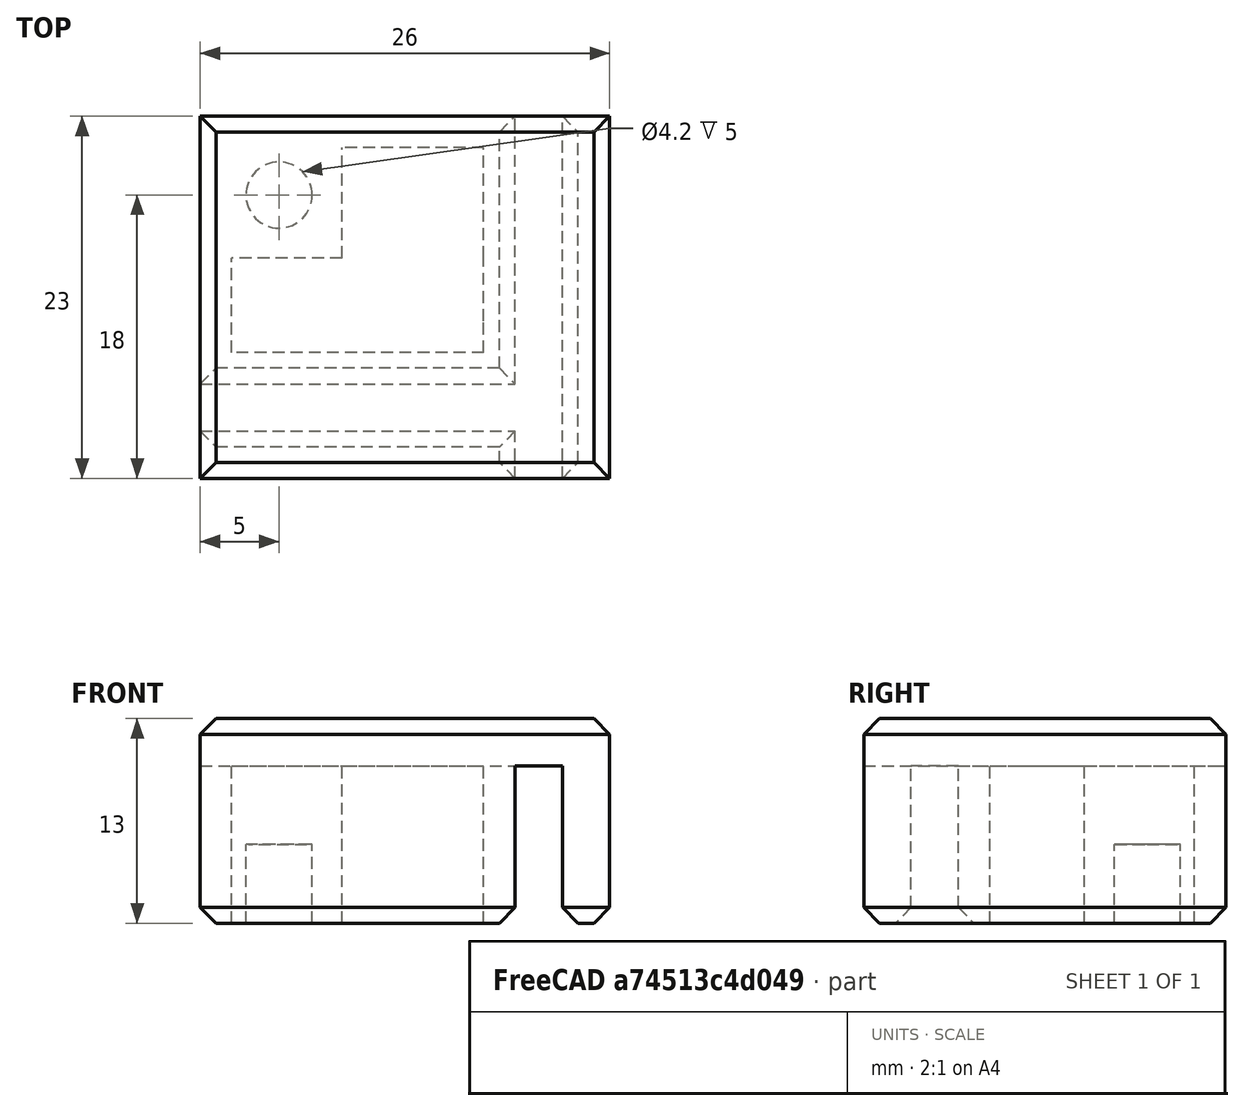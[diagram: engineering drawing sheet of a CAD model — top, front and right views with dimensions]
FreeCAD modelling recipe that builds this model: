
FCSTD DOCUMENT  (FreeCAD 0.16R6662 (Git))
Label: stangenhalter_eck
License: CreativeCommons Attribution-ShareAlike
LicenseURL: http://creativecommons.org/licenses/by-sa/4.0/
objects: Part::Cut×6, Part::Box×5, Part::Chamfer×3, Part::Cylinder×2
note: 16 computed .brp shape members not serialized (recipe doc carries the construction recipe); baked Part::Feature solids carry a one-line shape summary decoded from their .brp

FEATURE [Part::Box] Box  label="Cube"
  Height = 23
  Length = 26
  Placement = pos=(0,0,0) rot=(1,0,0;1.5708rad)
  Width = 13
FEATURE [Part::Cylinder] Cylinder
  Angle = 360
  Height = 10
  Placement = pos=(5,-5,-5) rot=(0,0,1;0rad)
  Radius = 2
FEATURE [Part::Box] Box001  label="Cube001"
  Height = 11
  Length = 3
  Placement = pos=(20,-24,-1) rot=(0,0,1;0rad)
  Width = 25
FEATURE [Part::Box] Box002  label="Cube002"
  Height = 11
  Length = 22
  Placement = pos=(-1,-20,-1) rot=(0,0,1;0rad)
  Width = 3
FEATURE [Part::Cut] Cut
  Base = -> Box
  Tool = -> Cylinder
FEATURE [Part::Cut] Cut001
  Base = -> Cut
  Tool = -> Box001
FEATURE [Part::Cut] Cut002
  Base = -> Cut001
  Tool = -> Box002
FEATURE [Part::Box] Box003  label="Cube003"
  Height = 11
  Length = 9
  Placement = pos=(9,-13,-1) rot=(0,0,1;0rad)
  Width = 11
FEATURE [Part::Box] Box004  label="Cube004"
  Height = 11
  Length = 16
  Placement = pos=(2,-15,-1) rot=(0,0,1;0rad)
  Width = 6
FEATURE [Part::Cut] Cut003
  Base = -> Cut002
  Tool = -> Box003
FEATURE [Part::Cut] Cut004
  Base = -> Cut003
  Tool = -> Box004
FEATURE [Part::Chamfer] Chamfer
  Base = -> Cut004
  Edges = 5 edges r=1: [Edge10,Edge11,Edge25,Edge27,Edge66]
FEATURE [Part::Chamfer] Chamfer001
  Base = -> Chamfer
  Edges = 7 edges r=1: [Edge1,Edge9,Edge11,Edge25,Edge39,Edge45,Edge72]
FEATURE [Part::Chamfer] Chamfer002
  Base = -> Chamfer001
  Edges = 4 edges r=1: [Edge3,Edge11,Edge19,Edge20]
FEATURE [Part::Cylinder] Cylinder001
  Angle = 360
  Height = 10
  Placement = pos=(5,-5,-5) rot=(0,0,1;0rad)
  Radius = 2.1
FEATURE [Part::Cut] Cut005
  Base = -> Chamfer002
  Tool = -> Cylinder001
